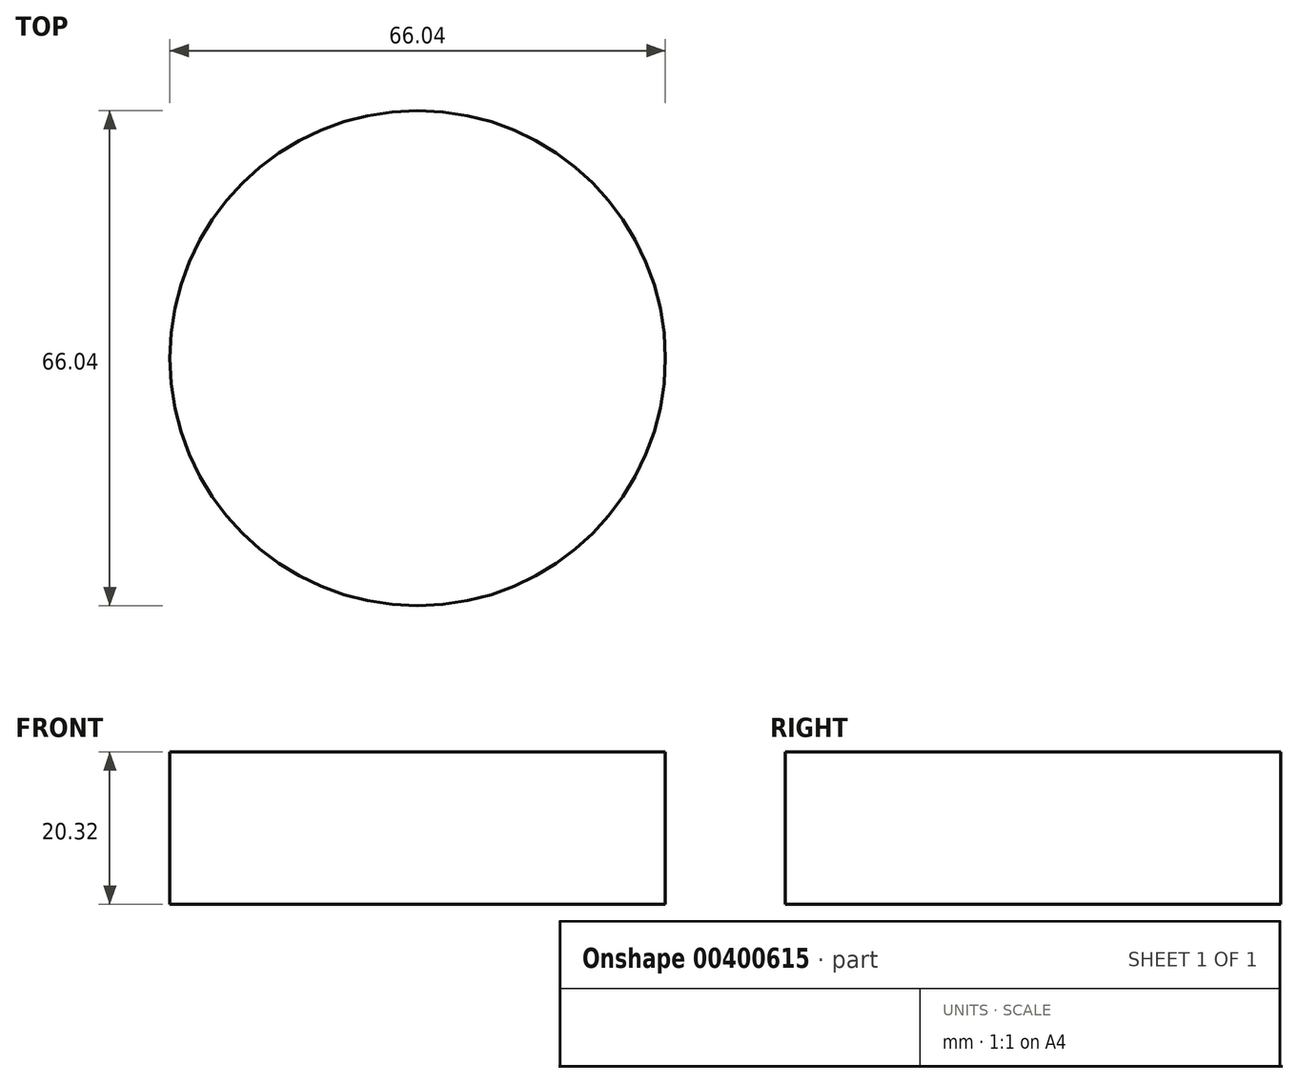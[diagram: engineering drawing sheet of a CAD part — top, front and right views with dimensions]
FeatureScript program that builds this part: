
annotation { "Feature Type Name" : "Feature", "Feature Type Description" : "" }
export const myFeature = defineFeature(function(context is Context, id is Id, definition is map)
    precondition{}
    {
        {
            var Q0;
            Q0=qCreatedBy(makeId("Top.planeOp"),FACE);
            var sketch = newSketch(context, id + "F0", { "sketchPlane" : qUnion([Q0])});
            skCircle(sketch, "E0", {"center": v(0, 0) * mm, "radius": 33.02 * mm});
            skSolve(sketch);
        }
        {
            assignVariable(context, id + "F1", {"name" : "ankerDepth", "anyValue" : 20.32 * mm});
        }
        {
            var Q0;
            Q0=makeQuery(id+"F0.imprint","IMPRINT",FACE,{"disambiguationData":[TD([[makeQuery(id+"F0.imprint","IMPRINT",EDGE,{"derivedFrom":sQuery(id+"F0.wireOp",EDGE,"E0")}),1.0]])]});
            extrude(context, id + "F2", {"entities" : qUnion([Q0]), "depth" : getVariable(context, 'ankerDepth')});
        }
    });
